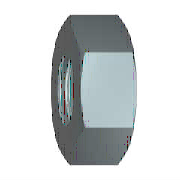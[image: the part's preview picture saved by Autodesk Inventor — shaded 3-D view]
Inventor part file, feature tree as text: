
AUTODESK INVENTOR PART (.ipt)
format: ipt  version: 2022 (Build 260153000, 153)  size: 174,592 bytes
history: native  units: mm (DEFAULTED — no unit token found)
features: sketch x3, chamfer x1, hole x1, other x1, plane x1
ambient origin geometry x7: Origin, YZ Plane, XZ Plane, X Axis, Y Axis, Z Axis, Center Point
bodies: Solid1 (feature_tree), Body (feature_tree)
feature tree (7):
  chamfer  "Chamfer1"  Angle=30.0deg  [1 undecoded]
  hole  "Thread"  [1 undecoded]
  other  "Work Axis1"
  plane  "Work Plane1"
  sketch  "Sketch1"  dims[d0=11.547005mm]
  sketch  "Sketch2"  dims[d1=5.2mm]
  sketch  "Sketch3"  dims[d2=0.0mm d3=30.0deg d4=30.0deg d5=10.0mm d6=10.0mm d7=90.0deg d25=4.917mm d26=6.0mm d27=4.0mm d28=2.0mm d29=14.3117mm d30=8.0mm d31=20.594885mm d8=0.541266mm d9=30.0deg d10=0.541266mm d11=30.0deg d13=0.0mm d14=0.0mm d39=0.0mm d40=0.541266mm d41=0.541266mm d42=0.0mm]
note: 2 required parameter values undecoded (feature->parameter linkage not recoverable at this tier; creation-order binding heuristic only, values carry confidence <= 0.55)
